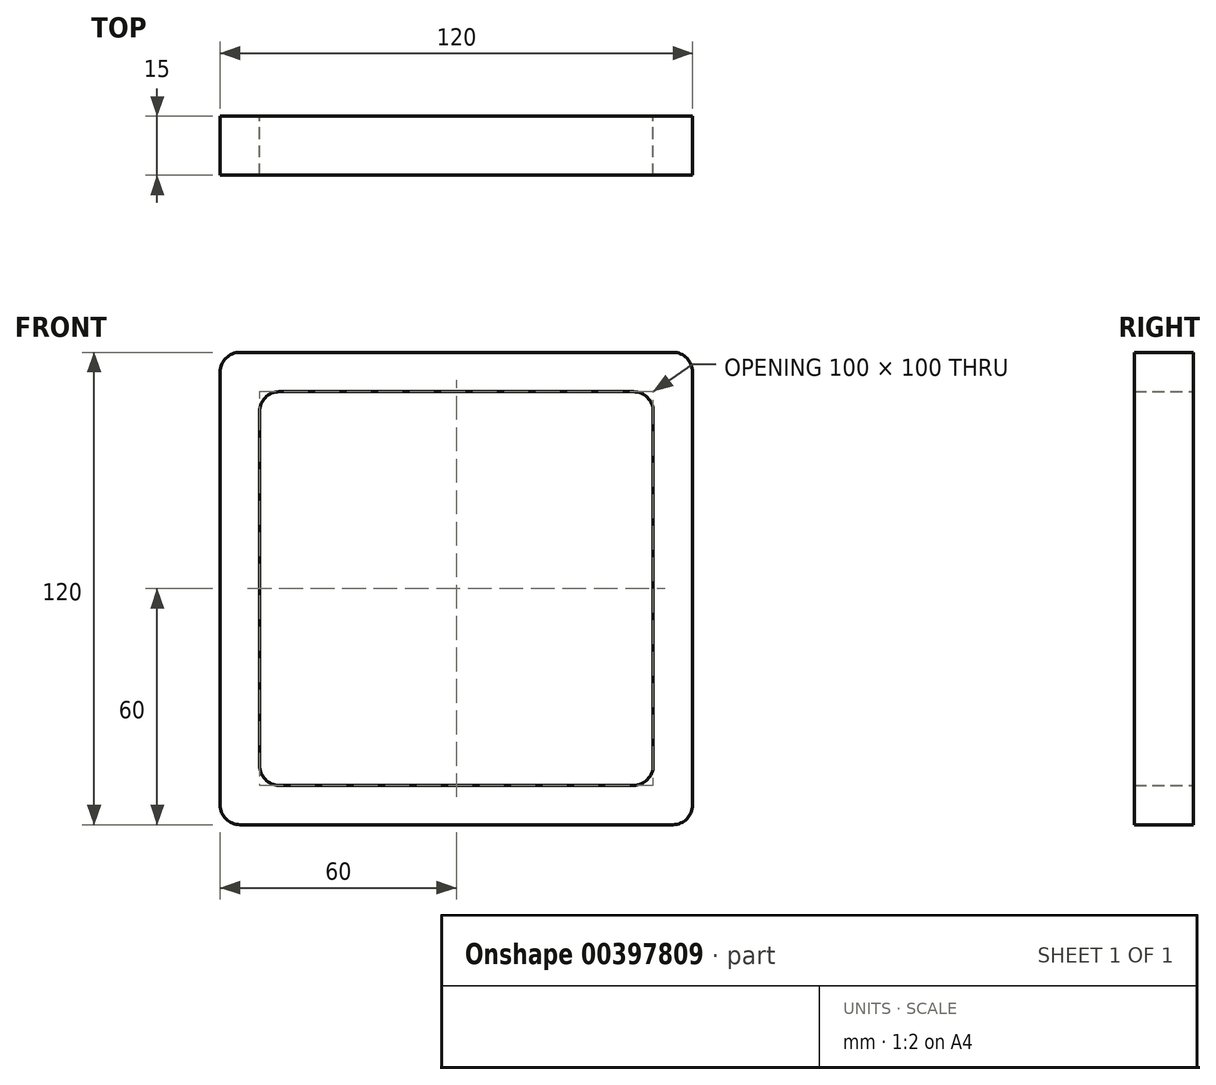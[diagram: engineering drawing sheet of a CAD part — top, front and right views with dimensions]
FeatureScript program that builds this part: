
annotation { "Feature Type Name" : "Feature", "Feature Type Description" : "" }
export const myFeature = defineFeature(function(context is Context, id is Id, definition is map)
    precondition{}
    {
        {
            var Q0;
            Q0=qCreatedBy(makeId("Front.planeOp"),FACE);
            var sketch = newSketch(context, id + "F0", { "sketchPlane" : qUnion([Q0])});
            skLineSegment(sketch, "E0", {"start": v(-45, 50) * mm, "end": v(45, 50) * mm});
            skLineSegment(sketch, "E1", {"start": v(50, 45) * mm, "end": v(50, -45) * mm});
            skLineSegment(sketch, "E2", {"start": v(45, -50) * mm, "end": v(-45, -50) * mm});
            skLineSegment(sketch, "E3", {"start": v(-50, -45) * mm, "end": v(-50, 45) * mm});
            skLineSegment(sketch, "E4", {"start": v(-60, 55) * mm, "end": v(-60, -55) * mm});
            skLineSegment(sketch, "E5", {"start": v(-55, 60) * mm, "end": v(55, 60) * mm});
            skLineSegment(sketch, "E6", {"start": v(60, 55) * mm, "end": v(60, -55) * mm});
            skLineSegment(sketch, "E7", {"start": v(0, 74.55) * mm, "end": v(0, -72.64) * mm, "construction": true});
            skLineSegment(sketch, "E8", {"start": v(75.52, 0) * mm, "end": v(-75.04, 0) * mm, "construction": true});
            skLineSegment(sketch, "E9", {"start": v(-55, -60) * mm, "end": v(55, -60) * mm});
            skPoint(sketch, "E10.orphan", {"position": v(60, -64.13) * mm});
            skPoint(sketch, "E11.visualSharp", {"position": v(-60, 60) * mm});
            skArc(sketch, "E11.filletArc", {"start": v(-55, 60) * mm, "mid": v(-58.54, 58.54) * mm, "end": v(-60, 55) * mm});
            skPoint(sketch, "E12.visualSharp", {"position": v(60, 60) * mm});
            skArc(sketch, "E12.filletArc", {"start": v(60, 55) * mm, "mid": v(58.54, 58.54) * mm, "end": v(55, 60) * mm});
            skPoint(sketch, "E13.visualSharp", {"position": v(60, -60) * mm});
            skArc(sketch, "E13.filletArc", {"start": v(55, -60) * mm, "mid": v(58.54, -58.54) * mm, "end": v(60, -55) * mm});
            skPoint(sketch, "E14.visualSharp", {"position": v(-60, -60) * mm});
            skArc(sketch, "E14.filletArc", {"start": v(-60, -55) * mm, "mid": v(-58.54, -58.54) * mm, "end": v(-55, -60) * mm});
            skPoint(sketch, "E15.visualSharp", {"position": v(-50, 50) * mm});
            skArc(sketch, "E15.filletArc", {"start": v(-45, 50) * mm, "mid": v(-48.54, 48.54) * mm, "end": v(-50, 45) * mm});
            skPoint(sketch, "E16.visualSharp", {"position": v(50, 50) * mm});
            skArc(sketch, "E16.filletArc", {"start": v(50, 45) * mm, "mid": v(48.54, 48.54) * mm, "end": v(45, 50) * mm});
            skPoint(sketch, "E17.visualSharp", {"position": v(50, -50) * mm});
            skArc(sketch, "E17.filletArc", {"start": v(45, -50) * mm, "mid": v(48.54, -48.54) * mm, "end": v(50, -45) * mm});
            skPoint(sketch, "E18.visualSharp", {"position": v(-50, -50) * mm});
            skArc(sketch, "E18.filletArc", {"start": v(-50, -45) * mm, "mid": v(-48.54, -48.54) * mm, "end": v(-45, -50) * mm});
            skSolve(sketch);
        }
        {
            var Q0;
            Q0 = qSketchRegion(id + "F0", true);
            extrude(context, id + "F1", {"entities" : qUnion([Q0]), "depth" : 15 * mm});
        }
    });
